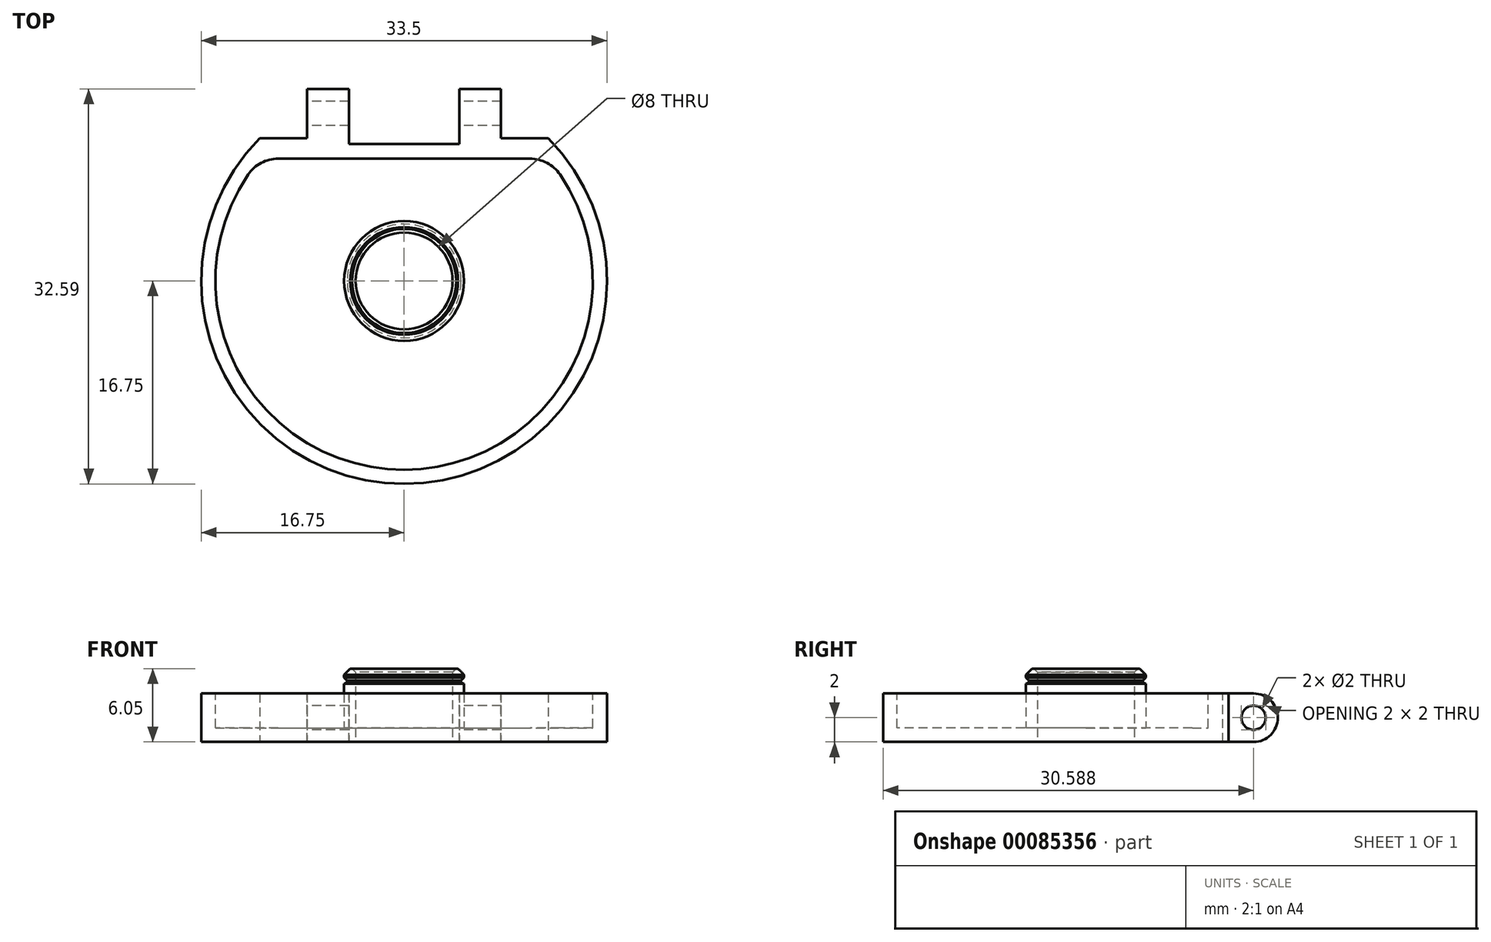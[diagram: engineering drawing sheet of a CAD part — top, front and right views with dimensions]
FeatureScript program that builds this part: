
annotation { "Feature Type Name" : "Feature", "Feature Type Description" : "" }
export const myFeature = defineFeature(function(context is Context, id is Id, definition is map)
    precondition{}
    {
        {
            var Q0;
            Q0=qCreatedBy(makeId("Top.planeOp"),FACE);
            var sketch = newSketch(context, id + "F0", { "sketchPlane" : qUnion([Q0])});
            skLineSegment(sketch, "E0", {"start": v(-11.9, 11.79) * mm, "end": v(11.9, 11.79) * mm});
            skArc(sketch, "E1", {"start": v(-12.51, 11.13) * mm, "mid": v(0.45, -16.74) * mm, "end": v(11.9, 11.79) * mm});
            skArc(sketch, "E2", {"start": v(-11.9, 11.79) * mm, "mid": v(-12.21, 11.46) * mm, "end": v(-12.51, 11.13) * mm});
            skSolve(sketch);
        }
        {
            var Q0;
            Q0=makeQuery(id+"F0.imprint","IMPRINT",FACE,{"disambiguationData":[TD([[makeQuery(id+"F0.imprint","IMPRINT",EDGE,{"derivedFrom":sQuery(id+"F0.wireOp",EDGE,"E0")}),-1.0]])]});
            extrude(context, id + "F1", {"entities" : qUnion([Q0]), "depth" : 4 * mm});
        }
        {
            var Q0;
            Q0=makeQuery(id+"F1.opExtrude","CAP_FACE",FACE,{"disambiguationData":[OSD([sQuery(id+"F0.wireOp",EDGE,"E0"),sQuery(id+"F0.wireOp",EDGE,"E1"),sQuery(id+"F0.wireOp",EDGE,"E2")])],"isStart":false});
            var sketch = newSketch(context, id + "F2", { "sketchPlane" : qUnion([Q0])});
            skArc(sketch, "E3", {"start": v(-11.87, 10.09) * mm, "mid": v(0, -15.58) * mm, "end": v(11.87, 10.09) * mm});
            skLineSegment(sketch, "E4", {"start": v(-11.87, 10.09) * mm, "end": v(11.87, 10.09) * mm});
            skSolve(sketch);
        }
        {
            var Q0;
            Q0 = qSketchRegion(id + "F2", true);
            extrude(context, id + "F3", {"entities" : qUnion([Q0]), "operationType" : NewBodyOperationType.REMOVE, "oppositeDirection" : true, "depth" : 2.83 * mm});
        }
        {
            var Q0;
            Q0=qCreatedBy(makeId("Front.planeOp"),FACE);
            var sketch = newSketch(context, id + "F4", { "sketchPlane" : qUnion([Q0])});
            skLineSegment(sketch, "E5.0.0", {"start": v(11.87, 1.17) * mm, "end": v(-11.87, 1.17) * mm});
            skLineSegment(sketch, "E5.0.1", {"start": v(-15.58, 1.17) * mm, "end": v(15.58, 1.17) * mm});
            skLineSegment(sketch, "E6", {"start": v(4.95, 1.17) * mm, "end": v(4.95, 4.8) * mm});
            skLineSegment(sketch, "E7", {"start": v(4.95, 4.8) * mm, "end": v(4.7, 4.9) * mm});
            skLineSegment(sketch, "E8", {"start": v(4.7, 4.9) * mm, "end": v(4.7, 5.05) * mm});
            skLineSegment(sketch, "E9", {"start": v(4.7, 5.05) * mm, "end": v(4.95, 5.3) * mm});
            skLineSegment(sketch, "E10", {"start": v(4.95, 5.3) * mm, "end": v(4.95, 6.05) * mm});
            skLineSegment(sketch, "E11", {"start": v(4.95, 6.05) * mm, "end": v(4, 6.05) * mm});
            skLineSegment(sketch, "E12", {"start": v(4, 6.05) * mm, "end": v(4, 1.17) * mm});
            skLineSegment(sketch, "E13", {"start": v(4, 1.17) * mm, "end": v(4.95, 1.17) * mm});
            skLineSegment(sketch, "E14", {"start": v(0, 4.61) * mm, "end": v(0, 6.94) * mm});
            skSolve(sketch);
        }
        {
            var Q0;
            Q0=makeQuery(id+"F4.imprint","IMPRINT",FACE,{"disambiguationData":[TD([[makeQuery(id+"F4.imprint","IMPRINT",EDGE,{"derivedFrom":sQuery(id+"F4.wireOp",EDGE,"E6")}),1.0]])]});
            var Q1;
            Q1=sQuery(id+"F4.wireOp",EDGE,"E14");
            revolve(context, id + "F5", {"operationType" : NewBodyOperationType.ADD, "entities" : qUnion([Q0]), "axis" : qUnion([Q1]), "revolveType" : RevolveType.FULL});
        }
        {
            var Q0;
            Q0=makeQuery(id+"F5.boolean.opBoolean","SPLIT",FACE,{"disambiguationData":[TD([makeQuery(id+"F5.opRevolve","SWEPT_FACE",FACE,{"disambiguationData":[OSD([sQuery(id+"F4.wireOp",EDGE,"E12")])]})])],"derivedFrom":makeQuery(id+"F3.boolean.opBoolean","COPY",FACE,{"derivedFrom":makeQuery(id+"F3.opExtrude","CAP_FACE",FACE,{"disambiguationData":[OSD([sQuery(id+"F2.wireOp",EDGE,"E3"),sQuery(id+"F2.wireOp",EDGE,"E4")])],"isStart":false})})});
            extrude(context, id + "F6", {"entities" : qUnion([Q0]), "operationType" : NewBodyOperationType.REMOVE, "endBound" : BoundingType.THROUGH_ALL, "oppositeDirection" : true, "depth" : 25 * mm});
        }
        {
            var Q0;
            Q0=makeQuery(id+"F5.opRevolve","SWEPT_EDGE",EDGE,{"disambiguationData":[OSD([sQuery(id+"F4.wireOp",EDGE,"E10"),sQuery(id+"F4.wireOp",EDGE,"E11")])]});
            chamfer(context, id + "F7", {"entities" : qUnion([Q0]), "width" : 0.5 * mm, "tangentPropagation" : true});
        }
        {
            var Q0;
            Q0=makeQuery(id+"F5.opRevolve","SWEPT_EDGE",EDGE,{"disambiguationData":[OSD([sQuery(id+"F4.wireOp",EDGE,"E11"),sQuery(id+"F4.wireOp",EDGE,"E12")])]});
            chamfer(context, id + "F8", {"entities" : qUnion([Q0]), "width" : 0.3 * mm, "tangentPropagation" : true});
        }
        {
            var Q0;
            Q0=qCreatedBy(makeId("Right.planeOp"),FACE);
            var sketch = newSketch(context, id + "F9", { "sketchPlane" : qUnion([Q0])});
            skLineSegment(sketch, "E15.0", {"start": v(11.79, 4) * mm, "end": v(11.79, 4) * mm});
            skLineSegment(sketch, "E16.0", {"start": v(11.79, 4) * mm, "end": v(11.79, 0) * mm});
            skLineSegment(sketch, "E17.bottom", {"start": v(11.79, 4) * mm, "end": v(13.84, 4) * mm});
            skLineSegment(sketch, "E17.top", {"start": v(11.79, 0) * mm, "end": v(13.84, 0) * mm});
            skPoint(sketch, "E18", {"position": v(13.84, 2) * mm});
            skArc(sketch, "E19", {"start": v(13.84, 4) * mm, "mid": v(15.84, 2) * mm, "end": v(13.84, 0) * mm});
            skCircle(sketch, "E20", {"center": v(13.84, 2) * mm, "radius": 1 * mm});
            skSolve(sketch);
        }
        {
            var Q0;
            Q0=makeQuery(id+"F9.imprint","IMPRINT",FACE,{"disambiguationData":[TD([[makeQuery(id+"F9.imprint","IMPRINT",EDGE,{"derivedFrom":sQuery(id+"F9.wireOp",EDGE,"E17.bottom")}),-1.0]])]});
            extrude(context, id + "F10", {"entities" : qUnion([Q0]), "operationType" : NewBodyOperationType.ADD, "depth" : 8 * mm, "hasSecondDirection" : true, "secondDirectionOppositeDirection" : true, "secondDirectionDepth" : 8 * mm});
        }
        {
            var Q0;
            {var subQ0=sQuery(id+"F9.wireOp",EDGE,"E17.bottom");var subQ3=sQuery(id+"F0.wireOp",EDGE,"E0");var subQ4=sQuery(id+"F9.wireOp",EDGE,"E17.top");Q0=makeQuery(id+"F10.boolean.opBoolean","SPLIT",FACE,{"disambiguationData":[TD([makeQuery(id+"F10.opExtrude","CAP_FACE",FACE,{"disambiguationData":[OSD([subQ0,subQ4,sQuery(id+"F9.wireOp",EDGE,"E16.0"),sQuery(id+"F9.wireOp",EDGE,"E19"),sQuery(id+"F9.wireOp",EDGE,"E20")])],"isStart":false})])],"derivedFrom":makeQuery(id+"F1.opExtrude","SWEPT_FACE",FACE,{"disambiguationData":[OSD([subQ3])]})});}
            var sketch = newSketch(context, id + "F11", { "sketchPlane" : qUnion([Q0])});
            skLineSegment(sketch, "E21.bottom", {"start": v(4.55, -0.8) * mm, "end": v(-4.55, -0.8) * mm});
            skLineSegment(sketch, "E21.top", {"start": v(4.55, 4.8) * mm, "end": v(-4.55, 4.8) * mm});
            skLineSegment(sketch, "E21.left", {"start": v(4.55, -0.8) * mm, "end": v(4.55, 4.8) * mm});
            skLineSegment(sketch, "E21.right", {"start": v(-4.55, -0.8) * mm, "end": v(-4.55, 4.8) * mm});
            skSolve(sketch);
        }
        {
            var Q0;
            Q0=makeQuery(id+"F11.imprint","IMPRINT",FACE,{"disambiguationData":[TD([[makeQuery(id+"F11.imprint","IMPRINT",EDGE,{"derivedFrom":sQuery(id+"F11.wireOp",EDGE,"E21.bottom")}),-1.0]])]});
            extrude(context, id + "F12", {"entities" : qUnion([Q0]), "operationType" : NewBodyOperationType.REMOVE, "oppositeDirection" : true, "depth" : 0.5 * mm, "hasSecondDirection" : true, "secondDirectionBound" : SecondDirectionBoundingType.THROUGH_ALL, "secondDirectionOppositeDirection" : false, "secondDirectionDepth" : 25 * mm});
        }
        {
            var Q0;
            {var subQ0=sQuery(id+"F2.wireOp",EDGE,"E4");var subQ1=sQuery(id+"F2.wireOp",EDGE,"E3");Q0=makeQuery(id+"F3.boolean.opBoolean","COPY",EDGE,{"derivedFrom":makeQuery(id+"F3.opExtrude","SWEPT_EDGE",EDGE,{"disambiguationData":[OSD([subQ1,subQ0]),TDD([makeQuery(id+"F2.imprint","INTERSECT",VERTEX,{"disambiguationData":[OD(0.0)],"derivedFrom":[subQ1,subQ0]})])]})});}
            var Q1;
            {var subQ0=sQuery(id+"F2.wireOp",EDGE,"E4");var subQ1=sQuery(id+"F2.wireOp",EDGE,"E3");Q1=makeQuery(id+"F3.boolean.opBoolean","COPY",EDGE,{"derivedFrom":makeQuery(id+"F3.opExtrude","SWEPT_EDGE",EDGE,{"disambiguationData":[OSD([subQ1,subQ0]),TDD([makeQuery(id+"F2.imprint","INTERSECT",VERTEX,{"disambiguationData":[OD(1.0)],"derivedFrom":[subQ1,subQ0]})])]})});}
            fillet(context, id + "F13", {"entities" : qUnion([Q0, Q1]), "tangentPropagation" : true, "radius" : 3 * mm, "defaultsChanged" : true, "vertexSettings" : [], "allowEdgeOverflow" : false});
        }
    });
